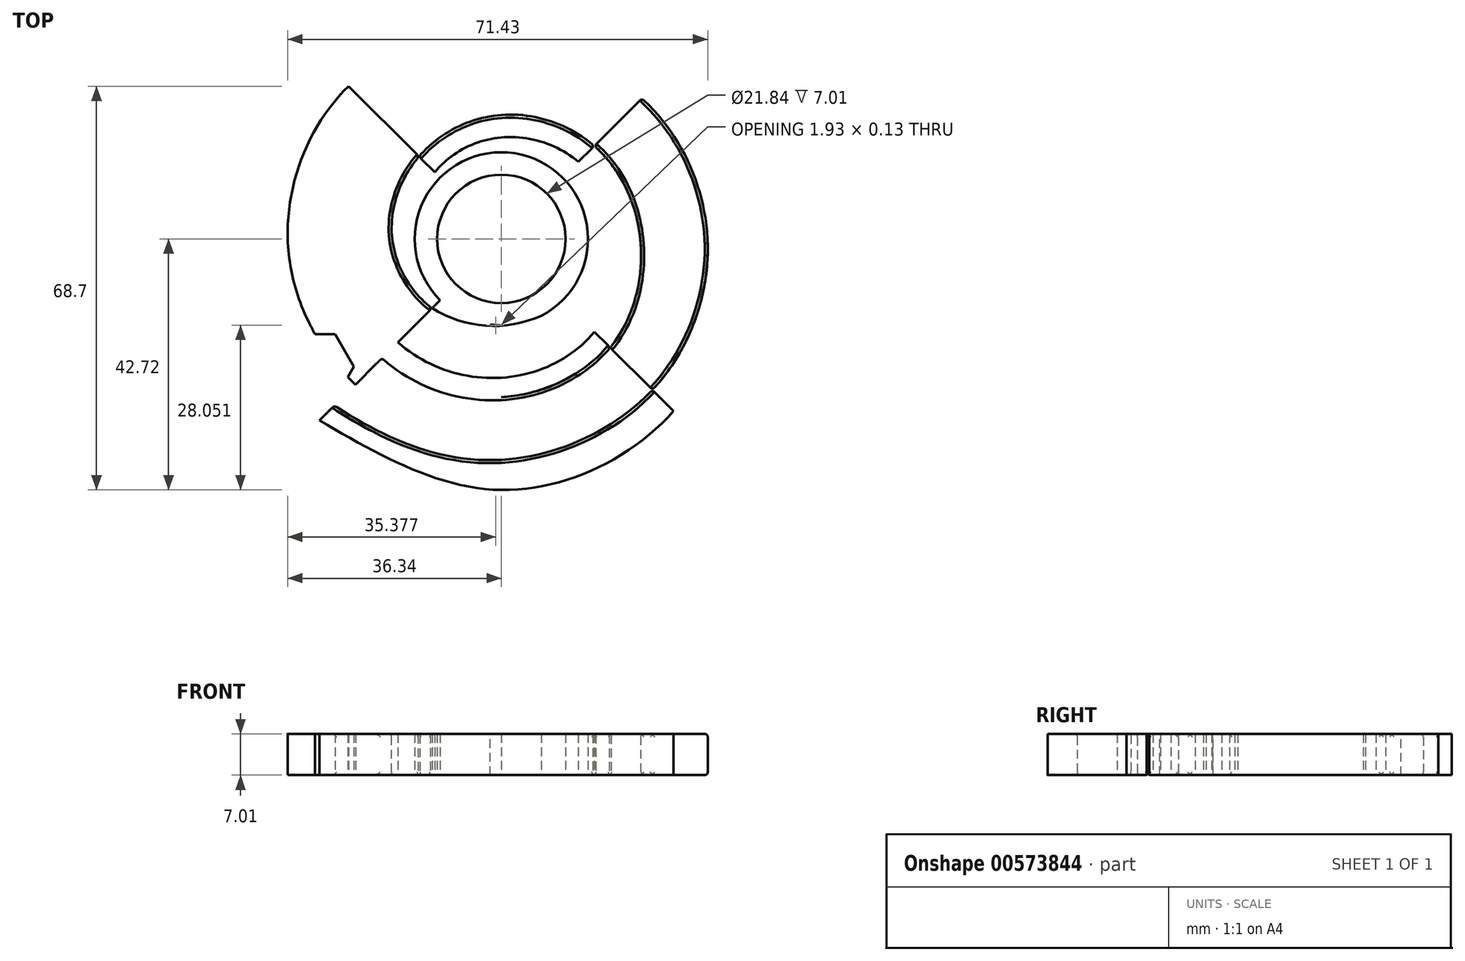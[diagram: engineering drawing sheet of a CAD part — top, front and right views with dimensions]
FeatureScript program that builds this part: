
annotation { "Feature Type Name" : "Feature", "Feature Type Description" : "" }
export const myFeature = defineFeature(function(context is Context, id is Id, definition is map)
    precondition{}
    {
        {
            var Q0;
            Q0=qCreatedBy(makeId("Top.planeOp"),FACE);
            var sketch = newSketch(context, id + "F0", { "sketchPlane" : qUnion([Q0])});
            skCircle(sketch, "E0", {"center": v(0, 0) * mm, "radius": 10.92 * mm});
            skLineSegment(sketch, "E1.MirrorCS", {"start": v(4.8, -76.2) * mm, "end": v(-4.8, -76.2) * mm});
            skLineSegment(sketch, "E2.MirrorCS", {"start": v(4.8, -73.66) * mm, "end": v(4.8, -76.2) * mm});
            skCircle(sketch, "E3", {"center": v(0, 0) * mm, "radius": 14.73 * mm});
            skLineSegment(sketch, "E4", {"start": v(-41.42, 0) * mm, "end": v(64.64, 0) * mm});
            skLineSegment(sketch, "E5", {"start": v(0, 42.25) * mm, "end": v(0, -46.64) * mm});
            skLineSegment(sketch, "E6", {"start": v(-32.56, -32.56) * mm, "end": v(44.86, 44.86) * mm});
            skLineSegment(sketch, "E7", {"start": v(40.79, -40.79) * mm, "end": v(-41, 41) * mm});
            skPoint(sketch, "E8", {"position": v(-11.76, -11.76) * mm});
            skPoint(sketch, "E9", {"position": v(-18.54, 0) * mm});
            skPoint(sketch, "E10", {"position": v(-14, 14) * mm});
            skPoint(sketch, "E11", {"position": v(0, 21.08) * mm});
            skPoint(sketch, "E12", {"position": v(15.8, 15.8) * mm});
            skPoint(sketch, "E13", {"position": v(23.62, 0) * mm});
            skPoint(sketch, "E14", {"position": v(18.5, -18.5) * mm});
            skPoint(sketch, "E15", {"position": v(0, -27.43) * mm});
            skPoint(sketch, "E16", {"position": v(-20.3, -20.3) * mm});
            skPoint(sketch, "E17", {"position": v(-29.97, 0) * mm});
            skPoint(sketch, "E18", {"position": v(-22.1, 22.1) * mm});
            skPoint(sketch, "E19", {"position": v(0, 32.51) * mm});
            skPoint(sketch, "E20", {"position": v(23.89, 23.89) * mm});
            skPoint(sketch, "E21", {"position": v(35.05, 0) * mm});
            skPoint(sketch, "E22", {"position": v(25.68, -25.68) * mm});
            skPoint(sketch, "E23", {"position": v(0, -37.6) * mm});
            skPoint(sketch, "E24", {"position": v(-28.38, -28.38) * mm});
            skFitSpline(sketch, "E25", {"points": [v(0, -14.73) * mm, v(-11.76, -11.76) * mm, v(-18.54, 0) * mm, v(-14, 14) * mm, v(0, 21.08) * mm, v(15.8, 15.8) * mm, v(23.62, 0) * mm, v(18.5, -18.5) * mm, v(0, -27.43) * mm, v(-20.3, -20.3) * mm, v(-29.97, 0) * mm, v(-22.1, 22.1) * mm, v(0, 32.51) * mm, v(23.89, 23.89) * mm, v(35.05, 0) * mm, v(25.68, -25.68) * mm, v(0, -37.6) * mm, v(-28.38, -28.38) * mm], "startDerivative": vector(-297.64, 16.93) * mm, "endDerivative": vector(-411.45, 267.75) * mm});
            skFitSpline(sketch, "E26.trimOffspring", {"points": [v(-30.9, -30.9) * mm, v(0, -42.72) * mm, v(29.3, -29.3) * mm, v(39.3, 0) * mm, v(27.16, 27.16) * mm, v(0, 36.05) * mm, v(-25.98, 25.98) * mm, v(-36.32, 0) * mm, v(-24.79, -24.79) * mm, v(0, -33.78) * mm, v(22.99, -22.99) * mm, v(31.24, 0) * mm, v(21.2, 21.2) * mm, v(0, 28.7) * mm, v(-19.4, 19.4) * mm, v(-26.16, 0) * mm, v(-17.6, -17.6) * mm, v(0, -23.62) * mm, v(15.8, -15.8) * mm, v(19.81, 0) * mm, v(13.11, 13.11) * mm, v(0, 17.27) * mm, v(-11.32, 11.32) * mm, v(-14.73, 0) * mm, v(-10.42, -10.42) * mm], "startDerivative": vector(577.9, -334.63) * mm, "endDerivative": vector(260.72, -309.12) * mm});
            skCircle(sketch, "E27", {"center": v(-31.43, -21.73) * mm, "radius": 4.36 * mm});
            skLineSegment(sketch, "E28", {"start": v(-14.4, -3.1) * mm, "end": v(-14.26, -3.1) * mm});
            skArc(sketch, "E29", {"start": v(-11.76, -11.76) * mm, "mid": v(-2.67, -14.77) * mm, "end": v(6.76, -13.09) * mm});
            skCircle(sketch, "E30.cCircle", {"center": v(-31.43, -21.73) * mm, "radius": 5.51 * mm, "construction": true});
            skLineSegment(sketch, "E30.0", {"start": v(-34.61, -16.22) * mm, "end": v(-28.25, -16.22) * mm});
            skLineSegment(sketch, "E30.1", {"start": v(-28.25, -16.22) * mm, "end": v(-25.07, -21.73) * mm});
            skLineSegment(sketch, "E30.2", {"start": v(-25.07, -21.73) * mm, "end": v(-28.25, -27.24) * mm});
            skLineSegment(sketch, "E30.3", {"start": v(-28.25, -27.24) * mm, "end": v(-34.61, -27.24) * mm});
            skLineSegment(sketch, "E30.4", {"start": v(-34.61, -27.24) * mm, "end": v(-37.8, -21.73) * mm});
            skLineSegment(sketch, "E30.5", {"start": v(-37.8, -21.73) * mm, "end": v(-34.61, -16.22) * mm});
            skPoint(sketch, "E30.0.midPoint", {"position": v(-31.43, -16.22) * mm});
            skArc(sketch, "E31", {"start": v(-24.79, -24.79) * mm, "mid": v(-36.7, -16.47) * mm, "end": v(-28.38, -28.38) * mm});
            skSolve(sketch);
        }
        {
            var Q0;
            {var subQ0=sQuery(id+"F0.wireOp",EDGE,"HUGIaErR-J9R2-Kyrz-Qgbt-Ax4g2k5T1JWC");Q0=makeQuery(id+"F0.imprint","IMPRINT",FACE,{"disambiguationData":[TD([[makeQuery(id+"F0.imprint","IMPRINT",EDGE,{"derivedFrom":subQ0}),1.0]])]});}
            var Q1;
            {var subQ0=sQuery(id+"F0.wireOp",EDGE,"E25");var subQ1=sQuery(id+"F0.wireOp",EDGE,"E4");var subQ2=makeQuery(id+"F0.imprint","INTERSECT",VERTEX,{"disambiguationData":[OD(0.0)],"derivedFrom":[subQ1,subQ0]});Q1=makeQuery(id+"F0.imprint","IMPRINT",FACE,{"disambiguationData":[TD([[makeQuery(id+"F0.imprint","IMPRINT",EDGE,{"disambiguationData":[TD([[subQ2,-1.0]])],"derivedFrom":subQ1}),-1.0]])]});}
            var Q2;
            {var subQ0=sQuery(id+"F0.wireOp",EDGE,"E25");var subQ1=sQuery(id+"F0.wireOp",EDGE,"E4");var subQ2=makeQuery(id+"F0.imprint","INTERSECT",VERTEX,{"disambiguationData":[OD(0.0)],"derivedFrom":[subQ1,subQ0]});Q2=makeQuery(id+"F0.imprint","IMPRINT",FACE,{"disambiguationData":[TD([[makeQuery(id+"F0.imprint","IMPRINT",EDGE,{"disambiguationData":[TD([[subQ2,-1.0]])],"derivedFrom":subQ1}),1.0]])]});}
            var Q3;
            {var subQ0=sQuery(id+"F0.wireOp",EDGE,"E25");var subQ1=sQuery(id+"F0.wireOp",EDGE,"E4");var subQ2=makeQuery(id+"F0.imprint","INTERSECT",VERTEX,{"disambiguationData":[OD(1.0)],"derivedFrom":[subQ1,subQ0]});Q3=makeQuery(id+"F0.imprint","IMPRINT",FACE,{"disambiguationData":[TD([[makeQuery(id+"F0.imprint","IMPRINT",EDGE,{"disambiguationData":[TD([[subQ2,1.0]])],"derivedFrom":subQ1}),1.0]])]});}
            var Q4;
            {var subQ0=sQuery(id+"F0.wireOp",EDGE,"E25");var subQ1=sQuery(id+"F0.wireOp",EDGE,"E4");var subQ2=makeQuery(id+"F0.imprint","INTERSECT",VERTEX,{"disambiguationData":[OD(1.0)],"derivedFrom":[subQ1,subQ0]});Q4=makeQuery(id+"F0.imprint","IMPRINT",FACE,{"disambiguationData":[TD([[makeQuery(id+"F0.imprint","IMPRINT",EDGE,{"disambiguationData":[TD([[subQ2,1.0]])],"derivedFrom":subQ1}),-1.0]])]});}
            var Q5;
            {var subQ0=sQuery(id+"F0.wireOp",EDGE,"E25");var subQ1=sQuery(id+"F0.wireOp",EDGE,"E5");var subQ2=makeQuery(id+"F0.imprint","INTERSECT",VERTEX,{"disambiguationData":[OD(0.0)],"derivedFrom":[subQ1,subQ0]});Q5=makeQuery(id+"F0.imprint","IMPRINT",FACE,{"disambiguationData":[TD([[makeQuery(id+"F0.imprint","IMPRINT",EDGE,{"disambiguationData":[TD([[subQ2,-1.0]])],"derivedFrom":subQ1}),1.0]])]});}
            var Q6;
            {var subQ0=sQuery(id+"F0.wireOp",EDGE,"E25");var subQ1=sQuery(id+"F0.wireOp",EDGE,"E5");var subQ2=makeQuery(id+"F0.imprint","INTERSECT",VERTEX,{"disambiguationData":[OD(0.0)],"derivedFrom":[subQ1,subQ0]});Q6=makeQuery(id+"F0.imprint","IMPRINT",FACE,{"disambiguationData":[TD([[makeQuery(id+"F0.imprint","IMPRINT",EDGE,{"disambiguationData":[TD([[subQ2,-1.0]])],"derivedFrom":subQ1}),-1.0]])]});}
            var Q7;
            {var subQ0=sQuery(id+"F0.wireOp",EDGE,"E25");var subQ1=sQuery(id+"F0.wireOp",EDGE,"E5");var subQ2=makeQuery(id+"F0.imprint","INTERSECT",VERTEX,{"disambiguationData":[OD(1.0)],"derivedFrom":[subQ1,subQ0]});Q7=makeQuery(id+"F0.imprint","IMPRINT",FACE,{"disambiguationData":[TD([[makeQuery(id+"F0.imprint","IMPRINT",EDGE,{"disambiguationData":[TD([[subQ2,1.0]])],"derivedFrom":subQ1}),-1.0]])]});}
            var Q8;
            {var subQ0=sQuery(id+"F0.wireOp",EDGE,"E25");var subQ1=sQuery(id+"F0.wireOp",EDGE,"E5");var subQ2=makeQuery(id+"F0.imprint","INTERSECT",VERTEX,{"disambiguationData":[OD(1.0)],"derivedFrom":[subQ1,subQ0]});Q8=makeQuery(id+"F0.imprint","IMPRINT",FACE,{"disambiguationData":[TD([[makeQuery(id+"F0.imprint","IMPRINT",EDGE,{"disambiguationData":[TD([[subQ2,1.0]])],"derivedFrom":subQ1}),1.0]])]});}
            var Q9;
            {var subQ0=sQuery(id+"F0.wireOp",EDGE,"E26.trimOffspring");var subQ1=sQuery(id+"F0.wireOp",EDGE,"E5");var subQ2=makeQuery(id+"F0.imprint","INTERSECT",VERTEX,{"disambiguationData":[OD(2.0)],"derivedFrom":[subQ1,subQ0]});Q9=makeQuery(id+"F0.imprint","IMPRINT",FACE,{"disambiguationData":[TD([[makeQuery(id+"F0.imprint","IMPRINT",EDGE,{"disambiguationData":[TD([[subQ2,-1.0]])],"derivedFrom":subQ1}),-1.0]])]});}
            var Q10;
            {var subQ0=sQuery(id+"F0.wireOp",EDGE,"E26.trimOffspring");var subQ1=sQuery(id+"F0.wireOp",EDGE,"E5");var subQ2=makeQuery(id+"F0.imprint","INTERSECT",VERTEX,{"disambiguationData":[OD(2.0)],"derivedFrom":[subQ1,subQ0]});Q10=makeQuery(id+"F0.imprint","IMPRINT",FACE,{"disambiguationData":[TD([[makeQuery(id+"F0.imprint","IMPRINT",EDGE,{"disambiguationData":[TD([[subQ2,-1.0]])],"derivedFrom":subQ1}),1.0]])]});}
            var Q11;
            {var subQ0=sQuery(id+"F0.wireOp",EDGE,"E26.trimOffspring");var subQ1=sQuery(id+"F0.wireOp",EDGE,"E4");var subQ2=makeQuery(id+"F0.imprint","INTERSECT",VERTEX,{"disambiguationData":[OD(2.0)],"derivedFrom":[subQ1,subQ0]});Q11=makeQuery(id+"F0.imprint","IMPRINT",FACE,{"disambiguationData":[TD([[makeQuery(id+"F0.imprint","IMPRINT",EDGE,{"disambiguationData":[TD([[subQ2,-1.0]])],"derivedFrom":subQ1}),-1.0]])]});}
            var Q12;
            {var subQ0=sQuery(id+"F0.wireOp",EDGE,"E26.trimOffspring");var subQ1=sQuery(id+"F0.wireOp",EDGE,"E4");var subQ2=makeQuery(id+"F0.imprint","INTERSECT",VERTEX,{"disambiguationData":[OD(2.0)],"derivedFrom":[subQ1,subQ0]});Q12=makeQuery(id+"F0.imprint","IMPRINT",FACE,{"disambiguationData":[TD([[makeQuery(id+"F0.imprint","IMPRINT",EDGE,{"disambiguationData":[TD([[subQ2,-1.0]])],"derivedFrom":subQ1}),1.0]])]});}
            var Q13;
            {var subQ0=sQuery(id+"F0.wireOp",EDGE,"E25");var subQ1=sQuery(id+"F0.wireOp",EDGE,"E5");var subQ2=makeQuery(id+"F0.imprint","INTERSECT",VERTEX,{"disambiguationData":[OD(2.0)],"derivedFrom":[subQ1,subQ0]});Q13=makeQuery(id+"F0.imprint","IMPRINT",FACE,{"disambiguationData":[TD([[makeQuery(id+"F0.imprint","IMPRINT",EDGE,{"disambiguationData":[TD([[subQ2,-1.0]])],"derivedFrom":subQ1}),1.0]])]});}
            var Q14;
            {var subQ0=sQuery(id+"F0.wireOp",EDGE,"E25");var subQ1=sQuery(id+"F0.wireOp",EDGE,"E5");var subQ2=makeQuery(id+"F0.imprint","INTERSECT",VERTEX,{"disambiguationData":[OD(2.0)],"derivedFrom":[subQ1,subQ0]});Q14=makeQuery(id+"F0.imprint","IMPRINT",FACE,{"disambiguationData":[TD([[makeQuery(id+"F0.imprint","IMPRINT",EDGE,{"disambiguationData":[TD([[subQ2,-1.0]])],"derivedFrom":subQ1}),-1.0]])]});}
            var Q15;
            {var subQ0=sQuery(id+"F0.wireOp",EDGE,"E25");var subQ1=sQuery(id+"F0.wireOp",EDGE,"E4");var subQ2=makeQuery(id+"F0.imprint","INTERSECT",VERTEX,{"disambiguationData":[OD(2.0)],"derivedFrom":[subQ1,subQ0]});Q15=makeQuery(id+"F0.imprint","IMPRINT",FACE,{"disambiguationData":[TD([[makeQuery(id+"F0.imprint","IMPRINT",EDGE,{"disambiguationData":[TD([[subQ2,-1.0]])],"derivedFrom":subQ1}),1.0]])]});}
            var Q16;
            {var subQ0=sQuery(id+"F0.wireOp",EDGE,"E25");var subQ1=sQuery(id+"F0.wireOp",EDGE,"E4");var subQ2=makeQuery(id+"F0.imprint","INTERSECT",VERTEX,{"disambiguationData":[OD(2.0)],"derivedFrom":[subQ1,subQ0]});Q16=makeQuery(id+"F0.imprint","IMPRINT",FACE,{"disambiguationData":[TD([[makeQuery(id+"F0.imprint","IMPRINT",EDGE,{"disambiguationData":[TD([[subQ2,-1.0]])],"derivedFrom":subQ1}),-1.0]])]});}
            var Q17;
            {var subQ1=sQuery(id+"F0.wireOp",EDGE,"E3");var subQ3=sQuery(id+"F0.wireOp",EDGE,"E25");var subQ4=makeQuery(id+"F0.imprint","INTERSECT",VERTEX,{"derivedFrom":[subQ1,subQ3]});Q17=makeQuery(id+"F0.imprint","IMPRINT",FACE,{"disambiguationData":[TD([[makeQuery(id+"F0.imprint","IMPRINT",EDGE,{"disambiguationData":[TD([[subQ4,-1.0]])],"derivedFrom":subQ3}),-1.0]])]});}
            var Q18;
            {var subQ0=sQuery(id+"F0.wireOp",EDGE,"E6");var subQ3=sQuery(id+"F0.wireOp",EDGE,"E0");var subQ4=makeQuery(id+"F0.imprint","INTERSECT",VERTEX,{"disambiguationData":[OD(1.0)],"derivedFrom":[subQ3,subQ0]});Q18=makeQuery(id+"F0.imprint","IMPRINT",FACE,{"disambiguationData":[TD([[makeQuery(id+"F0.imprint","IMPRINT",EDGE,{"disambiguationData":[TD([[subQ4,-1.0]])],"derivedFrom":subQ3}),-1.0]])]});}
            var Q19;
            {var subQ4=sQuery(id+"F0.wireOp",EDGE,"E0");var subQ6=sQuery(id+"F0.wireOp",EDGE,"E4");var subQ7=makeQuery(id+"F0.imprint","INTERSECT",VERTEX,{"disambiguationData":[OD(1.0)],"derivedFrom":[subQ4,subQ6]});Q19=makeQuery(id+"F0.imprint","IMPRINT",FACE,{"disambiguationData":[TD([[makeQuery(id+"F0.imprint","IMPRINT",EDGE,{"disambiguationData":[TD([[subQ7,-1.0]])],"derivedFrom":subQ4}),-1.0]])]});}
            var Q20;
            {var subQ0=sQuery(id+"F0.wireOp",EDGE,"E7");var subQ1=sQuery(id+"F0.wireOp",EDGE,"E0");var subQ2=makeQuery(id+"F0.imprint","INTERSECT",VERTEX,{"disambiguationData":[OD(0.0)],"derivedFrom":[subQ1,subQ0]});Q20=makeQuery(id+"F0.imprint","IMPRINT",FACE,{"disambiguationData":[TD([[makeQuery(id+"F0.imprint","IMPRINT",EDGE,{"disambiguationData":[TD([[subQ2,-1.0]])],"derivedFrom":subQ1}),-1.0]])]});}
            var Q21;
            {var subQ0=sQuery(id+"F0.wireOp",EDGE,"E6");var subQ1=sQuery(id+"F0.wireOp",EDGE,"E0");var subQ2=makeQuery(id+"F0.imprint","INTERSECT",VERTEX,{"disambiguationData":[OD(0.0)],"derivedFrom":[subQ1,subQ0]});Q21=makeQuery(id+"F0.imprint","IMPRINT",FACE,{"disambiguationData":[TD([[makeQuery(id+"F0.imprint","IMPRINT",EDGE,{"disambiguationData":[TD([[subQ2,-1.0]])],"derivedFrom":subQ1}),-1.0]])]});}
            var Q22;
            {var subQ0=sQuery(id+"F0.wireOp",EDGE,"E4");var subQ1=sQuery(id+"F0.wireOp",EDGE,"E0");var subQ2=makeQuery(id+"F0.imprint","INTERSECT",VERTEX,{"disambiguationData":[OD(0.0)],"derivedFrom":[subQ1,subQ0]});Q22=makeQuery(id+"F0.imprint","IMPRINT",FACE,{"disambiguationData":[TD([[makeQuery(id+"F0.imprint","IMPRINT",EDGE,{"disambiguationData":[TD([[subQ2,1.0]])],"derivedFrom":subQ1}),-1.0]])]});}
            var Q23;
            {var subQ0=sQuery(id+"F0.wireOp",EDGE,"E5");var subQ1=sQuery(id+"F0.wireOp",EDGE,"E0");var subQ2=makeQuery(id+"F0.imprint","INTERSECT",VERTEX,{"disambiguationData":[OD(0.0)],"derivedFrom":[subQ1,subQ0]});Q23=makeQuery(id+"F0.imprint","IMPRINT",FACE,{"disambiguationData":[TD([[makeQuery(id+"F0.imprint","IMPRINT",EDGE,{"disambiguationData":[TD([[subQ2,-1.0]])],"derivedFrom":subQ1}),-1.0]])]});}
            var Q24;
            {var subQ0=sQuery(id+"F0.wireOp",EDGE,"E6");var subQ1=sQuery(id+"F0.wireOp",EDGE,"E0");var subQ2=makeQuery(id+"F0.imprint","INTERSECT",VERTEX,{"disambiguationData":[OD(0.0)],"derivedFrom":[subQ1,subQ0]});Q24=makeQuery(id+"F0.imprint","IMPRINT",FACE,{"disambiguationData":[TD([[makeQuery(id+"F0.imprint","IMPRINT",EDGE,{"disambiguationData":[TD([[subQ2,1.0]])],"derivedFrom":subQ1}),-1.0]])]});}
            var Q25;
            {var subQ0=sQuery(id+"F0.wireOp",EDGE,"E28");Q25=makeQuery(id+"F0.imprint","IMPRINT",FACE,{"disambiguationData":[TD([[makeQuery(id+"F0.imprint","IMPRINT",EDGE,{"derivedFrom":subQ0}),-1.0]])]});}
            var Q26;
            {var subQ0=sQuery(id+"F0.wireOp",EDGE,"E26.trimOffspring");var subQ1=sQuery(id+"F0.wireOp",EDGE,"E3");var subQ3=makeQuery(id+"F0.imprint","INTERSECT",VERTEX,{"derivedFrom":[subQ1,subQ0]});Q26=makeQuery(id+"F0.imprint","IMPRINT",FACE,{"disambiguationData":[TD([[makeQuery(id+"F0.imprint","IMPRINT",EDGE,{"disambiguationData":[TD([[subQ3,-1.0]])],"derivedFrom":subQ1}),1.0]])]});}
            var Q27;
            {var subQ0=sQuery(id+"F0.wireOp",EDGE,"E25");var subQ2=sQuery(id+"F0.wireOp",EDGE,"E3");var subQ4=makeQuery(id+"F0.imprint","INTERSECT",VERTEX,{"derivedFrom":[subQ2,subQ0]});Q27=makeQuery(id+"F0.imprint","IMPRINT",FACE,{"disambiguationData":[TD([[makeQuery(id+"F0.imprint","IMPRINT",EDGE,{"disambiguationData":[TD([[subQ4,-1.0]])],"derivedFrom":subQ0}),1.0]])]});}
            var Q28;
            {var subQ0=sQuery(id+"F0.wireOp",EDGE,"E5");var subQ3=sQuery(id+"F0.wireOp",EDGE,"E0");var subQ4=makeQuery(id+"F0.imprint","INTERSECT",VERTEX,{"disambiguationData":[OD(1.0)],"derivedFrom":[subQ3,subQ0]});Q28=makeQuery(id+"F0.imprint","IMPRINT",FACE,{"disambiguationData":[TD([[makeQuery(id+"F0.imprint","IMPRINT",EDGE,{"disambiguationData":[TD([[subQ4,-1.0]])],"derivedFrom":subQ3}),-1.0]])]});}
            var Q29;
            {var subQ1=sQuery(id+"F0.wireOp",EDGE,"E3");var subQ3=sQuery(id+"F0.wireOp",EDGE,"E29");var subQ4=makeQuery(id+"F0.imprint","INTERSECT",VERTEX,{"disambiguationData":[OD(1.0)],"derivedFrom":[subQ1,subQ3]});Q29=makeQuery(id+"F0.imprint","IMPRINT",FACE,{"disambiguationData":[TD([[makeQuery(id+"F0.imprint","IMPRINT",EDGE,{"disambiguationData":[TD([[subQ4,1.0]])],"derivedFrom":subQ3}),1.0]])]});}
            var Q30;
            {var subQ0=sQuery(id+"F0.wireOp",EDGE,"E26.trimOffspring");var subQ1=sQuery(id+"F0.wireOp",EDGE,"E4");var subQ2=makeQuery(id+"F0.imprint","INTERSECT",VERTEX,{"disambiguationData":[OD(1.0)],"derivedFrom":[subQ1,subQ0]});Q30=makeQuery(id+"F0.imprint","IMPRINT",FACE,{"disambiguationData":[TD([[makeQuery(id+"F0.imprint","IMPRINT",EDGE,{"disambiguationData":[TD([[subQ2,-1.0]])],"derivedFrom":subQ1}),1.0]])]});}
            var Q31;
            {var subQ0=sQuery(id+"F0.wireOp",EDGE,"E26.trimOffspring");var subQ1=sQuery(id+"F0.wireOp",EDGE,"E4");var subQ2=makeQuery(id+"F0.imprint","INTERSECT",VERTEX,{"disambiguationData":[OD(1.0)],"derivedFrom":[subQ1,subQ0]});Q31=makeQuery(id+"F0.imprint","IMPRINT",FACE,{"disambiguationData":[TD([[makeQuery(id+"F0.imprint","IMPRINT",EDGE,{"disambiguationData":[TD([[subQ2,-1.0]])],"derivedFrom":subQ1}),-1.0]])]});}
            var Q32;
            Q32=makeQuery(id+"F0.imprint","IMPRINT",FACE,{"disambiguationData":[TD([[makeQuery(id+"F0.imprint","IMPRINT",EDGE,{"derivedFrom":sQuery(id+"F0.wireOp",EDGE,"E30.0")}),1.0]])]});
            extrude(context, id + "F1", {"entities" : qUnion([Q0, Q1, Q2, Q3, Q4, Q5, Q6, Q7, Q8, Q9, Q10, Q11, Q12, Q13, Q14, Q15, Q16, Q17, Q18, Q19, Q20, Q21, Q22, Q23, Q24, Q25, Q26, Q27, Q28, Q29, Q30, Q31, Q32]), "depth" : 7 * mm, "offsetDistance" : 25.4 * mm});
        }
        {
            var Q0;
            {var subQ0=sQuery(id+"F0.wireOp",EDGE,"E25");var subQ1=sQuery(id+"F0.wireOp",EDGE,"E6");var subQ2=sQuery(id+"F0.wireOp",EDGE,"E5");var subQ3=makeQuery(id+"F0.imprint","INTERSECT",VERTEX,{"disambiguationData":[OD(1.0)],"derivedFrom":[subQ2,subQ0]});var subQ6=sQuery(id+"F0.wireOp",EDGE,"E4");var subQ7=makeQuery(id+"F0.imprint","INTERSECT",VERTEX,{"disambiguationData":[OD(1.0)],"derivedFrom":[subQ6,subQ0]});var subQ9=makeQuery(id+"F0.imprint","INTERSECT",VERTEX,{"disambiguationData":[OD(0.0)],"derivedFrom":[subQ2,subQ0]});var subQ11=makeQuery(id+"F0.imprint","INTERSECT",VERTEX,{"disambiguationData":[OD(0.0)],"derivedFrom":[subQ6,subQ0]});var subQ12=makeQuery(id+"F0.imprint","INTERSECT",VERTEX,{"disambiguationData":[OD(1.0)],"derivedFrom":[subQ1,subQ0]});var subQ13=makeQuery(id+"F0.imprint","INTERSECT",VERTEX,{"disambiguationData":[OD(3.0)],"derivedFrom":[subQ2,subQ0]});var subQ15=makeQuery(id+"F0.imprint","INTERSECT",VERTEX,{"disambiguationData":[OD(3.0)],"derivedFrom":[subQ6,subQ0]});var subQ17=makeQuery(id+"F0.imprint","INTERSECT",VERTEX,{"disambiguationData":[OD(2.0)],"derivedFrom":[subQ2,subQ0]});var subQ19=makeQuery(id+"F0.imprint","INTERSECT",VERTEX,{"disambiguationData":[OD(2.0)],"derivedFrom":[subQ6,subQ0]});Q0=makeQuery(id+"F1.opExtrude","SWEPT_FACE",FACE,{"disambiguationData":[OSD([subQ0]),TDD([makeQuery(id+"F0.imprint","IMPRINT",EDGE,{"disambiguationData":[TD([[subQ19,1.0]])],"derivedFrom":subQ0}),makeQuery(id+"F0.imprint","IMPRINT",EDGE,{"disambiguationData":[TD([[subQ19,-1.0]])],"derivedFrom":subQ0}),makeQuery(id+"F0.imprint","IMPRINT",EDGE,{"disambiguationData":[TD([[subQ17,1.0]])],"derivedFrom":subQ0}),makeQuery(id+"F0.imprint","IMPRINT",EDGE,{"disambiguationData":[TD([[subQ17,-1.0]])],"derivedFrom":subQ0}),makeQuery(id+"F0.imprint","IMPRINT",EDGE,{"disambiguationData":[TD([[subQ15,1.0]])],"derivedFrom":subQ0}),makeQuery(id+"F0.imprint","IMPRINT",EDGE,{"disambiguationData":[TD([[subQ15,-1.0]])],"derivedFrom":subQ0}),makeQuery(id+"F0.imprint","IMPRINT",EDGE,{"disambiguationData":[TD([[subQ13,1.0]])],"derivedFrom":subQ0}),makeQuery(id+"F0.imprint","IMPRINT",EDGE,{"disambiguationData":[TD([[subQ12,1.0]])],"derivedFrom":subQ0}),makeQuery(id+"F0.imprint","IMPRINT",EDGE,{"disambiguationData":[TD([[subQ11,1.0]])],"derivedFrom":subQ0}),makeQuery(id+"F0.imprint","IMPRINT",EDGE,{"disambiguationData":[TD([[subQ11,-1.0]])],"derivedFrom":subQ0}),makeQuery(id+"F0.imprint","IMPRINT",EDGE,{"disambiguationData":[TD([[subQ9,1.0]])],"derivedFrom":subQ0}),makeQuery(id+"F0.imprint","IMPRINT",EDGE,{"disambiguationData":[TD([[subQ9,-1.0]])],"derivedFrom":subQ0}),makeQuery(id+"F0.imprint","IMPRINT",EDGE,{"disambiguationData":[TD([[subQ7,1.0]])],"derivedFrom":subQ0}),makeQuery(id+"F0.imprint","IMPRINT",EDGE,{"disambiguationData":[TD([[subQ7,-1.0]])],"derivedFrom":subQ0}),makeQuery(id+"F0.imprint","IMPRINT",EDGE,{"disambiguationData":[TD([[subQ3,1.0]])],"derivedFrom":subQ0}),makeQuery(id+"F0.imprint","IMPRINT",EDGE,{"disambiguationData":[TD([[subQ3,-1.0]])],"derivedFrom":subQ0})])]});}
            var Q1;
            Q1=makeQuery(id+"F1.opExtrude","SWEPT_FACE",FACE,{"disambiguationData":[OSD([sQuery(id+"F0.wireOp",EDGE,"E29")])]});
            var Q2;
            {var subQ0=sQuery(id+"F0.wireOp",EDGE,"E4");var subQ1=sQuery(id+"F0.wireOp",EDGE,"E3");var subQ2=makeQuery(id+"F0.imprint","INTERSECT",VERTEX,{"disambiguationData":[OD(0.0)],"derivedFrom":[subQ1,subQ0]});var subQ3=sQuery(id+"F0.wireOp",EDGE,"E7");var subQ6=makeQuery(id+"F0.imprint","INTERSECT",VERTEX,{"disambiguationData":[OD(0.0)],"derivedFrom":[subQ1,subQ3]});var subQ7=makeQuery(id+"F0.imprint","INTERSECT",VERTEX,{"derivedFrom":[subQ1,sQuery(id+"F0.wireOp",EDGE,"E5")]});var subQ8=makeQuery(id+"F0.imprint","INTERSECT",VERTEX,{"derivedFrom":[subQ1,sQuery(id+"F0.wireOp",EDGE,"E6")]});Q2=makeQuery(id+"F1.opExtrude","SWEPT_FACE",FACE,{"disambiguationData":[OSD([subQ1]),TDD([makeQuery(id+"F0.imprint","IMPRINT",EDGE,{"disambiguationData":[TD([[subQ8,1.0]])],"derivedFrom":subQ1}),makeQuery(id+"F0.imprint","IMPRINT",EDGE,{"disambiguationData":[TD([[subQ8,-1.0]])],"derivedFrom":subQ1}),makeQuery(id+"F0.imprint","IMPRINT",EDGE,{"disambiguationData":[TD([[subQ7,-1.0]])],"derivedFrom":subQ1}),makeQuery(id+"F0.imprint","IMPRINT",EDGE,{"disambiguationData":[TD([[subQ6,-1.0]])],"derivedFrom":subQ1}),makeQuery(id+"F0.imprint","IMPRINT",EDGE,{"disambiguationData":[TD([[makeQuery(id+"F0.imprint","INTERSECT",VERTEX,{"derivedFrom":[subQ1,sQuery(id+"F0.wireOp",EDGE,"E28")]}),1.0]])],"derivedFrom":subQ1}),makeQuery(id+"F0.imprint","IMPRINT",EDGE,{"disambiguationData":[TD([[makeQuery(id+"F0.imprint","INTERSECT",VERTEX,{"disambiguationData":[OD(0.0)],"derivedFrom":[subQ1,sQuery(id+"F0.wireOp",EDGE,"E29")]}),-1.0]])],"derivedFrom":subQ1}),makeQuery(id+"F0.imprint","IMPRINT",EDGE,{"disambiguationData":[TD([[subQ2,1.0]])],"derivedFrom":subQ1})])]});}
            var Q3;
            Q3=makeQuery(id+"F1.opExtrude","SWEPT_FACE",FACE,{"disambiguationData":[OSD([sQuery(id+"F0.wireOp",EDGE,"HUGIaErR-J9R2-Kyrz-Qgbt-Ax4g2k5T1JWC")])]});
            fillet(context, id + "F2", {"entities" : qUnion([Q0, Q1, Q2, Q3]), "radius" : 0.5 * mm, "tangentPropagation" : true, "allowEdgeOverflow" : false});
        }
    });
